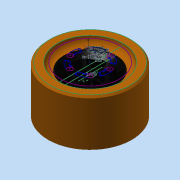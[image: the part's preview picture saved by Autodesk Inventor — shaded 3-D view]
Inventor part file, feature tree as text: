
AUTODESK INVENTOR PART (.ipt)
format: ipt  version: 2014 (Build 180170000, 170)  size: 467,456 bytes
history: native  units: in
note: dims shown in document units (in); Inventor stores cm internally (conversion verified against a paired STEP export)
features: other x3, sketch x2, projected_geometry x1
ambient origin geometry x8: Origin, YZ Plane, XZ Plane, XY Plane, X Axis, Y Axis, Z Axis, Center Point
bodies: Solid1 (feature_tree)
feature tree (6):
  other  "wheel90mm.ipt"
  sketch  "Sketch1"  dims[d0=0.3937in]
  sketch  "Sketch2"  dims[d4=0.0197in d7=0.205in d18=0.015in d19=0.03in d23=0.025in d28=2.48in d29=0.025in d30=0.025in d31=0.11in d32=0.03in d33=120.0deg d34=120.0deg d36=0.035in d37=2.3622in d39=360.0deg d41=0.05in]
  other  "Solid1::wheel90mm.ipt"
  other  "TaggingFeature1"
  projected_geometry  "Projected Loop1"
